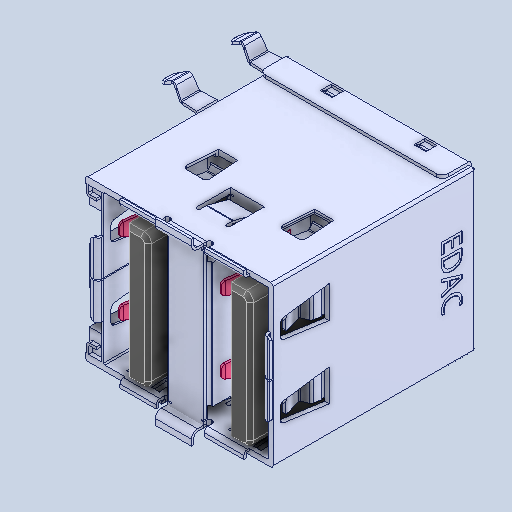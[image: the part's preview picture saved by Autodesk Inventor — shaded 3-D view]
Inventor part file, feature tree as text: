
AUTODESK INVENTOR PART (.ipt)
format: ipt  version: 2022 (Build 260153000, 153)  size: 1,743,360 bytes
history: mixed  units: in
note: dims shown in document units (in); Inventor stores cm internally (conversion verified against a paired STEP export)
features: other x20, mirror x7, fillet x4, chamfer x2, imported_body x1
ambient origin geometry x8: Origin, YZ Plane, XZ Plane, XY Plane, X Axis, Y Axis, Z Axis, Center Point
bodies: Solid1 (imported_parasolid), Solid2 (imported_parasolid), Solid3 (imported_parasolid), Solid4 (imported_parasolid), Solid5 (imported_parasolid), Solid6 (imported_parasolid), Solid7 (imported_parasolid), Solid8 (imported_parasolid), Solid9 (imported_parasolid), Solid10 (imported_parasolid), Solid11 (imported_parasolid), Solid12 (imported_parasolid), Solid13 (imported_parasolid), Solid14 (imported_parasolid), Solid15 (imported_parasolid), Solid16 (imported_parasolid), Solid17 (imported_parasolid), Solid18 (imported_parasolid), Solid19 (imported_parasolid), Solid20 (imported_parasolid), Solid21 (imported_parasolid), Solid22 (imported_parasolid), Solid23 (imported_parasolid), Solid24 (imported_parasolid), Solid25 (imported_parasolid), Solid26 (imported_parasolid), Solid27 (imported_parasolid), Solid28 (imported_parasolid), Solid29 (imported_parasolid), Solid30 (imported_parasolid), Solid31 (imported_parasolid), Solid32 (imported_parasolid), Solid33 (imported_parasolid)
feature tree (34):
  other  "Cut-Extrude5[1]"
  other  "Cut-Extrude5[2]"
  other  "Cut-Extrude5[3]"
  other  "Cut-Extrude5[4]"
  other  "Cut-Extrude7[1]"
  other  "Cut-Extrude7[2]"
  other  "Cut-Extrude11[3]"
  other  "Cut-Extrude11[4]"
  mirror  "Mirror7[1]"
  mirror  "Mirror7[2]"
  other  "Cut-Extrude13[1]"
  other  "Cut-Extrude13[2]"
  mirror  "Mirror8[1]"
  mirror  "Mirror8[2]"
  chamfer  "Chamfer4"  [1 undecoded]
  chamfer  "Chamfer5"  [1 undecoded]
  other  "Boss-Extrude14"
  other  "LPattern1"
  mirror  "Mirror9[1]"
  mirror  "Mirror9[2]"
  other  "LPattern2[1]"
  other  "LPattern2[2]"
  other  "LPattern2[3]"
  other  "LPattern2[4]"
  other  "LPattern3[1]"
  other  "LPattern3[2]"
  other  "Cut-Extrude15"
  mirror  "Mirror10"
  fillet  "Fillet4"  [1 undecoded]
  fillet  "Fillet5"  [1 undecoded]
  fillet  "Fillet6"  [1 undecoded]
  fillet  "Fillet7"  [1 undecoded]
  other  "Wytnij-wyciągnięcie1"
  imported_body  NMx_Import_Brep_tag  [imported B-rep: ~36 faces, bbox_mm=None]
note: 6 required parameter values undecoded (feature->parameter linkage not recoverable at this tier; creation-order binding heuristic only, values carry confidence <= 0.55)
